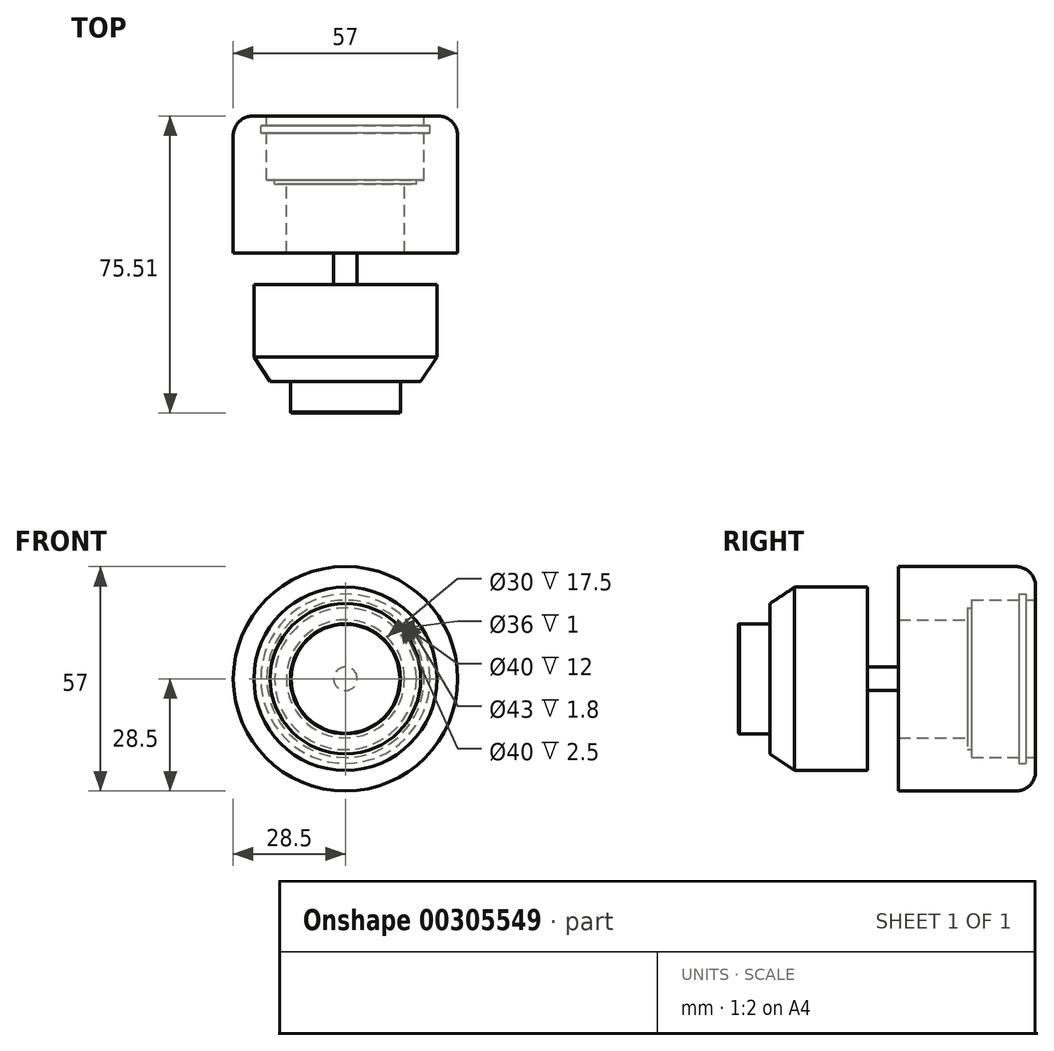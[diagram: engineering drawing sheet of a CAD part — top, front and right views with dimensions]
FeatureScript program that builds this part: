
annotation { "Feature Type Name" : "Feature", "Feature Type Description" : "" }
export const myFeature = defineFeature(function(context is Context, id is Id, definition is map)
    precondition{}
    {
        {
            var Q0;
            Q0=qCreatedBy(makeId("Front.planeOp"),FACE);
            var sketch = newSketch(context, id + "F0", { "sketchPlane" : qUnion([Q0])});
            skCircle(sketch, "E0", {"center": v(0, 0) * mm, "radius": 3 * mm});
            skSolve(sketch);
        }
        {
            var Q0;
            Q0=makeQuery(id+"F0.imprint","IMPRINT",FACE,{"disambiguationData":[TD([[makeQuery(id+"F0.imprint","IMPRINT",EDGE,{"derivedFrom":sQuery(id+"F0.wireOp",EDGE,"E0")}),1.0]])]});
            extrude(context, id + "F1", {"entities" : qUnion([Q0]), "depth" : 20 * mm});
        }
        {
            var Q0;
            Q0=qCreatedBy(makeId("Right.planeOp"),FACE);
            var sketch = newSketch(context, id + "F2", { "sketchPlane" : qUnion([Q0])});
            skLineSegment(sketch, "E1", {"start": v(0, 15) * mm, "end": v(0, 28.5) * mm});
            skLineSegment(sketch, "E2", {"start": v(0, 28.5) * mm, "end": v(34.8, 28.5) * mm});
            skLineSegment(sketch, "E3", {"start": v(34.8, 28.5) * mm, "end": v(34.8, 20) * mm});
            skLineSegment(sketch, "E4", {"start": v(34.8, 20) * mm, "end": v(32.3, 20) * mm});
            skLineSegment(sketch, "E5", {"start": v(32.3, 20) * mm, "end": v(32.3, 21.5) * mm});
            skLineSegment(sketch, "E6", {"start": v(32.3, 21.5) * mm, "end": v(30.5, 21.5) * mm});
            skLineSegment(sketch, "E7", {"start": v(30.5, 21.5) * mm, "end": v(30.5, 20) * mm});
            skLineSegment(sketch, "E8", {"start": v(30.5, 20) * mm, "end": v(18.5, 20) * mm});
            skLineSegment(sketch, "E9", {"start": v(18.5, 20) * mm, "end": v(18.5, 18) * mm});
            skLineSegment(sketch, "E10", {"start": v(18.5, 18) * mm, "end": v(17.5, 18) * mm});
            skLineSegment(sketch, "E11", {"start": v(17.5, 18) * mm, "end": v(17.5, 15) * mm});
            skLineSegment(sketch, "E12", {"start": v(17.5, 15) * mm, "end": v(0, 15) * mm});
            skSolve(sketch);
        }
        {
            var Q0;
            Q0=makeQuery(id+"F2.imprint","IMPRINT",FACE,{"disambiguationData":[TD([[makeQuery(id+"F2.imprint","IMPRINT",EDGE,{"derivedFrom":sQuery(id+"F2.wireOp",EDGE,"E1")}),-1.0]])]});
            var Q1;
            Q1=makeQuery(id+"F1.opExtrude","CAP_EDGE",EDGE,{"disambiguationData":[OSD([sQuery(id+"F0.wireOp",EDGE,"E0")])],"isStart":false});
            revolve(context, id + "F3", {"entities" : qUnion([Q0]), "axis" : qUnion([Q1]), "revolveType" : RevolveType.FULL});
        }
        {
            var Q0;
            Q0=qCreatedBy(makeId("Right.planeOp"),FACE);
            var sketch = newSketch(context, id + "F4", { "sketchPlane" : qUnion([Q0])});
            skLineSegment(sketch, "E13", {"start": v(-7.99, 0) * mm, "end": v(-7.99, 23.27) * mm});
            skLineSegment(sketch, "E14", {"start": v(-7.99, 23.27) * mm, "end": v(-32.7, 23.27) * mm});
            skLineSegment(sketch, "E15", {"start": v(-32.7, 23.27) * mm, "end": v(-32.7, 13.98) * mm});
            skLineSegment(sketch, "E16", {"start": v(-32.7, 13.98) * mm, "end": v(-40.71, 13.98) * mm});
            skLineSegment(sketch, "E17", {"start": v(-40.71, 13.98) * mm, "end": v(-40.71, 0) * mm});
            skLineSegment(sketch, "E18", {"start": v(-40.71, 0) * mm, "end": v(-7.99, 0) * mm});
            skSolve(sketch);
        }
        {
            var Q0;
            Q0=makeQuery(id+"F4.imprint","IMPRINT",FACE,{"disambiguationData":[TD([[makeQuery(id+"F4.imprint","IMPRINT",EDGE,{"derivedFrom":sQuery(id+"F4.wireOp",EDGE,"E13")}),1.0]])]});
            var Q1;
            Q1=sQuery(id+"F4.wireOp",EDGE,"E18");
            revolve(context, id + "F5", {"operationType" : NewBodyOperationType.ADD, "entities" : qUnion([Q0]), "axis" : qUnion([Q1]), "revolveType" : RevolveType.FULL});
        }
        {
            var Q0;
            Q0=qCreatedBy(makeId("Right.planeOp"),FACE);
            var sketch = newSketch(context, id + "F6", { "sketchPlane" : qUnion([Q0])});
            skLineSegment(sketch, "E19", {"start": v(-4.85, 37.5) * mm, "end": v(-42.7, 37.5) * mm});
            skLineSegment(sketch, "E20", {"start": v(-42.7, 37.5) * mm, "end": v(-42.7, 12.5) * mm});
            skLineSegment(sketch, "E21", {"start": v(-42.7, 12.5) * mm, "end": v(-4.85, 37.5) * mm});
            skSolve(sketch);
        }
        {
            var Q0;
            Q0=makeQuery(id+"F6.imprint","IMPRINT",FACE,{"disambiguationData":[TD([[makeQuery(id+"F6.imprint","IMPRINT",EDGE,{"derivedFrom":sQuery(id+"F6.wireOp",EDGE,"E19")}),1.0]])]});
            var Q1;
            Q1=makeQuery(id+"F3.opRevolve","SWEPT_EDGE",EDGE,{"disambiguationData":[OSD([sQuery(id+"F2.wireOp",EDGE,"E1"),sQuery(id+"F2.wireOp",EDGE,"E12")])]});
            revolve(context, id + "F7", {"operationType" : NewBodyOperationType.REMOVE, "entities" : qUnion([Q0]), "axis" : qUnion([Q1]), "revolveType" : RevolveType.FULL, "oppositeDirection" : true});
        }
        {
            var Q0;
            Q0=makeQuery(id+"F3.opRevolve","SWEPT_EDGE",EDGE,{"disambiguationData":[OSD([sQuery(id+"F2.wireOp",EDGE,"E2"),sQuery(id+"F2.wireOp",EDGE,"E3")])]});
            fillet(context, id + "F8", {"entities" : qUnion([Q0]), "radius" : 5 * mm, "tangentPropagation" : true, "allowEdgeOverflow" : false});
        }
    });
